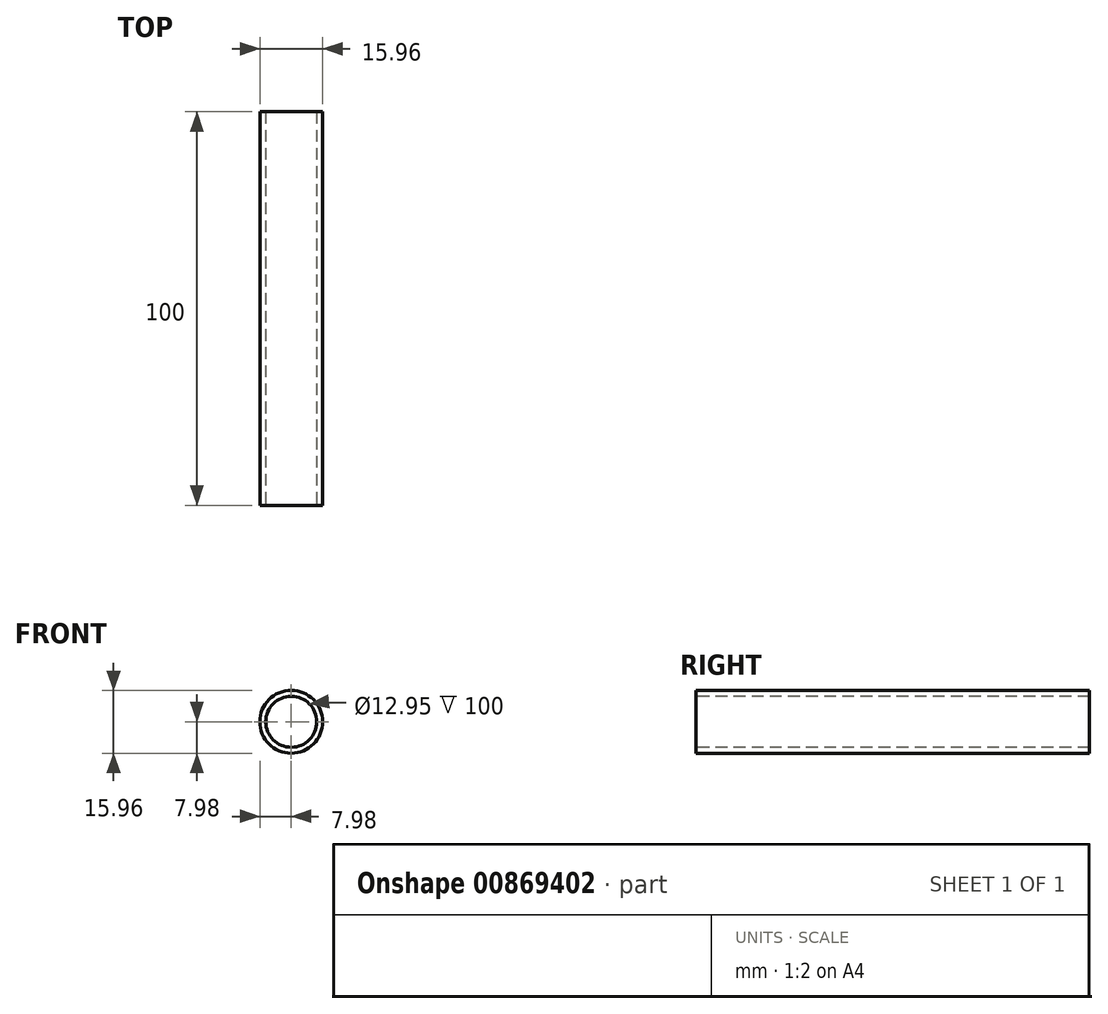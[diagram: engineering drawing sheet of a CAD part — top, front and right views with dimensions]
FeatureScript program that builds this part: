
annotation { "Feature Type Name" : "Feature", "Feature Type Description" : "" }
export const myFeature = defineFeature(function(context is Context, id is Id, definition is map)
    precondition{}
    {
        {
            var Q0;
            Q0=qCreatedBy(makeId("Front.planeOp"),FACE);
            var sketch = newSketch(context, id + "F0", { "sketchPlane" : qUnion([Q0])});
            skCircle(sketch, "E0", {"center": v(0, 0) * mm, "radius": 7.97 * mm});
            skCircle(sketch, "E1", {"center": v(0, 0) * mm, "radius": 6.47 * mm});
            skSolve(sketch);
        }
        {
            var Q0;
            Q0=makeQuery(id+"F0.imprint","IMPRINT",FACE,{"disambiguationData":[TD([[makeQuery(id+"F0.imprint","IMPRINT",EDGE,{"derivedFrom":sQuery(id+"F0.wireOp",EDGE,"E0")}),1.0]])]});
            extrude(context, id + "F1", {"entities" : qUnion([Q0]), "oppositeDirection" : true, "depth" : 100 * mm, "offsetDistance" : 25 * mm});
        }
    });
